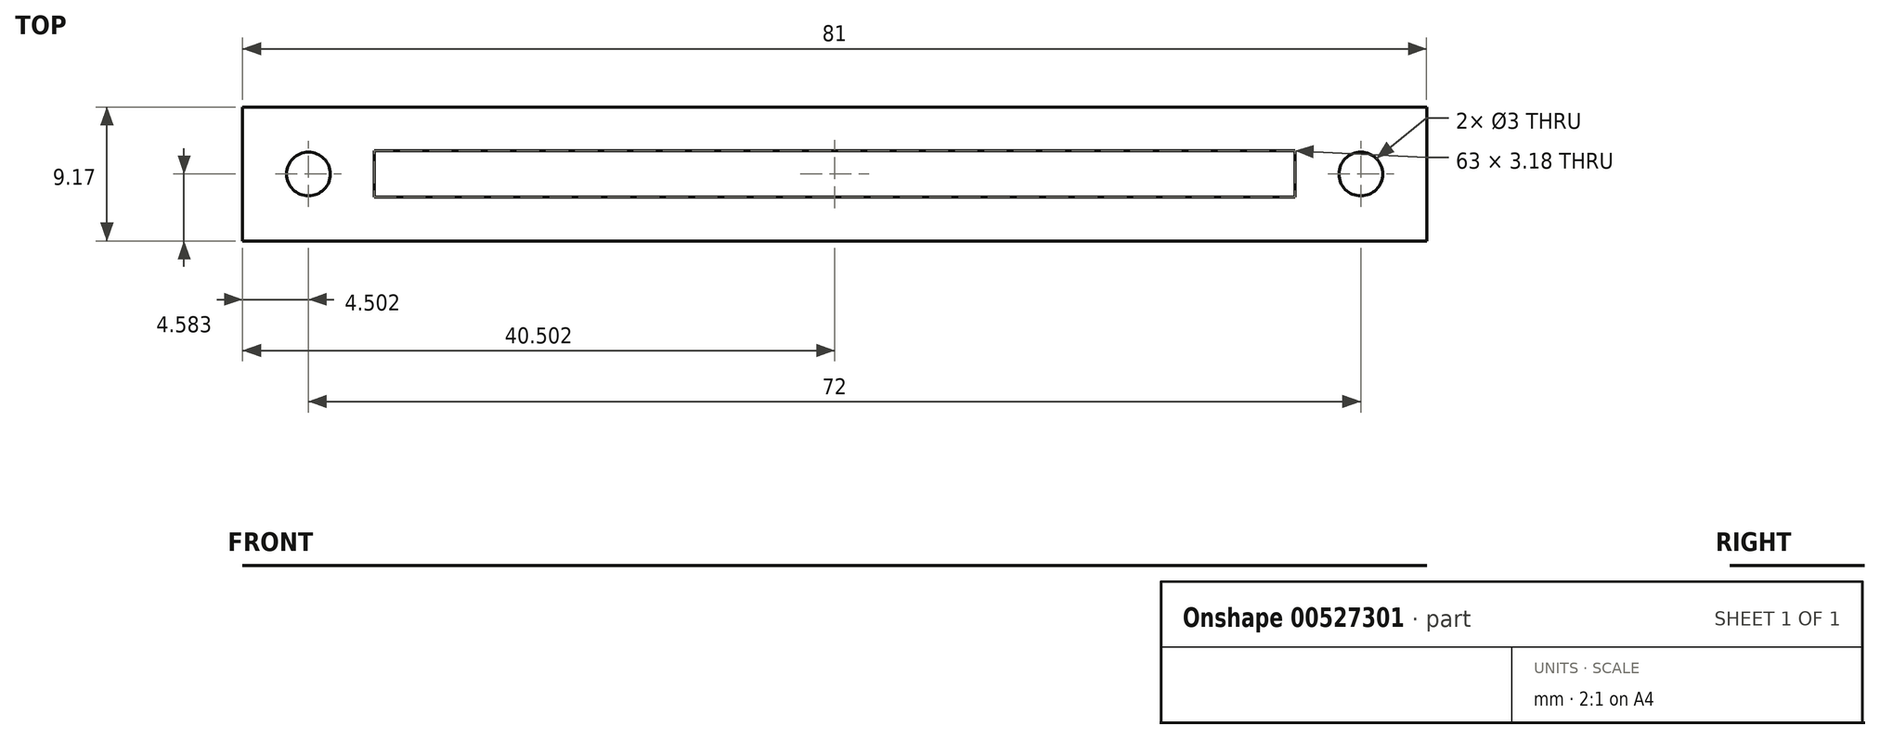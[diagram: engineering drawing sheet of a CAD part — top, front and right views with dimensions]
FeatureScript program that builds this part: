
annotation { "Feature Type Name" : "Feature", "Feature Type Description" : "" }
export const myFeature = defineFeature(function(context is Context, id is Id, definition is map)
    precondition{}
    {
        {
            var Q0;
            Q0=qCreatedBy(makeId("Top.planeOp"),FACE);
            var sketch = newSketch(context, id + "F0", { "sketchPlane" : qUnion([Q0])});
            skLineSegment(sketch, "E0.bottom", {"start": v(3.92, 18.22) * mm, "end": v(66.92, 18.22) * mm});
            skLineSegment(sketch, "E0.top", {"start": v(3.92, 15.05) * mm, "end": v(66.92, 15.05) * mm});
            skLineSegment(sketch, "E0.left", {"start": v(3.92, 18.22) * mm, "end": v(3.92, 15.05) * mm});
            skLineSegment(sketch, "E0.right", {"start": v(66.92, 18.22) * mm, "end": v(66.92, 15.05) * mm});
            skPoint(sketch, "E0.middle", {"position": v(35.42, 16.63) * mm});
            skCircle(sketch, "E1", {"center": v(-0.58, 16.63) * mm, "radius": 1.5 * mm});
            skLineSegment(sketch, "E2", {"start": v(35.42, 16.63) * mm, "end": v(35.42, 18.22) * mm});
            skCircle(sketch, "E3.MirrorC", {"center": v(71.42, 16.63) * mm, "radius": 1.5 * mm});
            skLineSegment(sketch, "E4.bottom", {"start": v(-5.08, 12.05) * mm, "end": v(75.92, 12.05) * mm});
            skLineSegment(sketch, "E4.top", {"start": v(-5.08, 21.22) * mm, "end": v(75.92, 21.22) * mm});
            skLineSegment(sketch, "E4.left", {"start": v(-5.08, 12.05) * mm, "end": v(-5.08, 21.22) * mm});
            skLineSegment(sketch, "E4.right", {"start": v(75.92, 12.05) * mm, "end": v(75.92, 21.22) * mm});
            skSolve(sketch);
        }
        {
            var Q0;
            Q0=makeQuery(id+"F0.imprint","IMPRINT",FACE,{"disambiguationData":[TD([[makeQuery(id+"F0.imprint","IMPRINT",EDGE,{"derivedFrom":sQuery(id+"F0.wireOp",EDGE,"E0.top")}),-1.0]])]});
            extrude(context, id + "F1", {"entities" : qUnion([Q0]), "depth" : 1 / 203.2 * mm, "offsetDistance" : 25 * mm});
        }
    });
